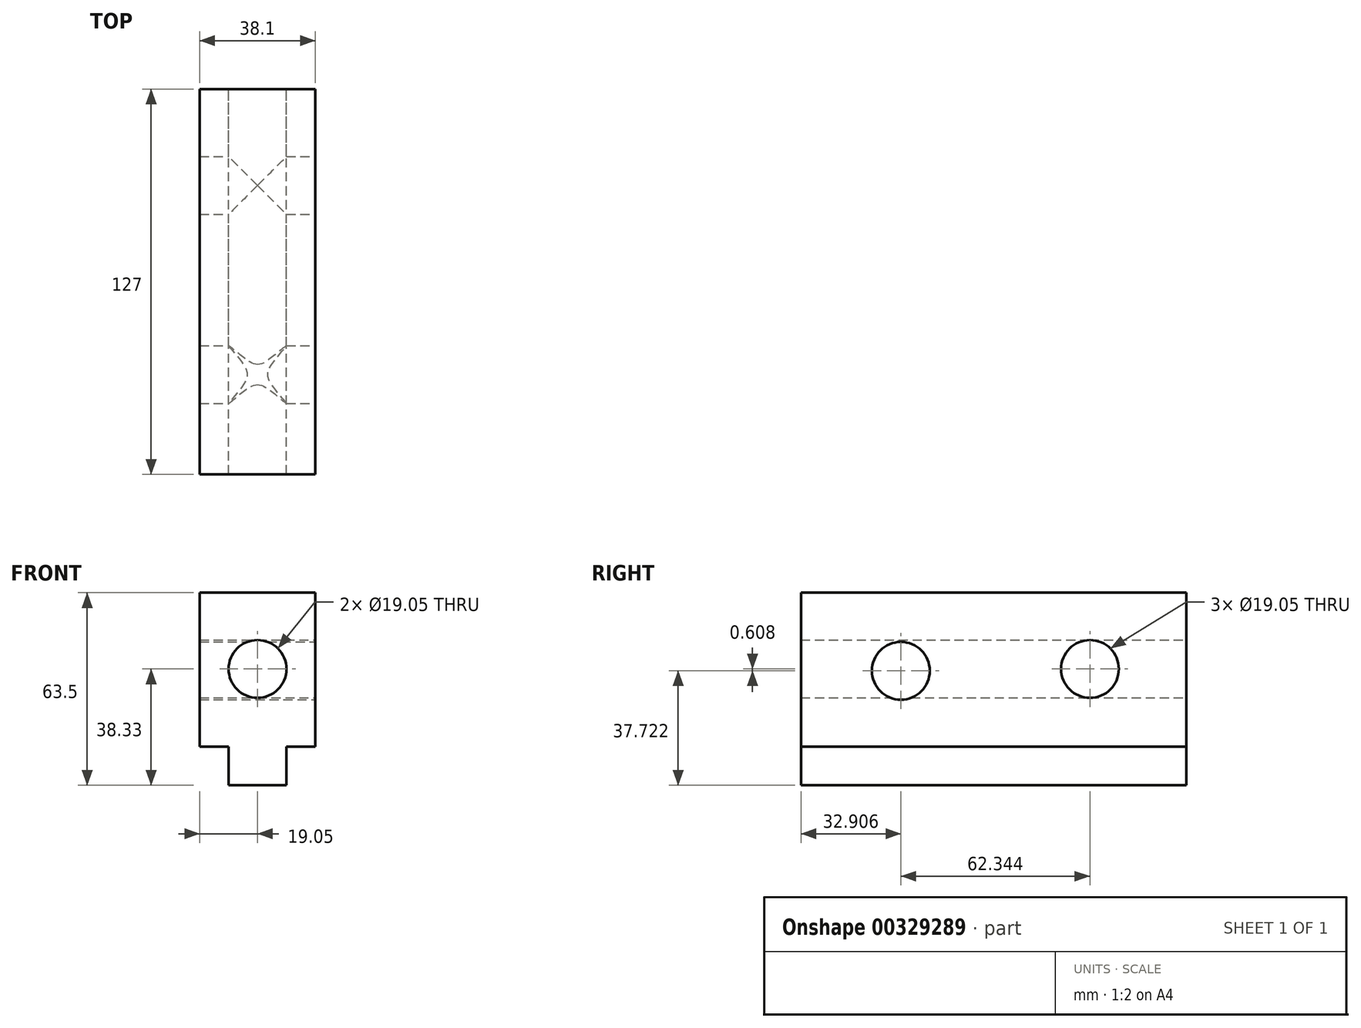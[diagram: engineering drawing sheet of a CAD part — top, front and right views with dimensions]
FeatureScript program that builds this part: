
annotation { "Feature Type Name" : "Feature", "Feature Type Description" : "" }
export const myFeature = defineFeature(function(context is Context, id is Id, definition is map)
    precondition{}
    {
        {
            var Q0;
            Q0=qCreatedBy(makeId("Front.planeOp"),FACE);
            var sketch = newSketch(context, id + "F0", { "sketchPlane" : qUnion([Q0])});
            skLineSegment(sketch, "E0", {"start": v(-28.57, -38.33) * mm, "end": v(-9.53, -38.33) * mm});
            skLineSegment(sketch, "E1", {"start": v(-28.57, -38.33) * mm, "end": v(-28.57, -25.63) * mm});
            skLineSegment(sketch, "E2", {"start": v(-9.53, -38.33) * mm, "end": v(-9.53, -25.63) * mm});
            skLineSegment(sketch, "E3", {"start": v(-9.53, -25.63) * mm, "end": v(0, -25.63) * mm});
            skLineSegment(sketch, "E4", {"start": v(-28.57, -25.63) * mm, "end": v(-38.1, -25.63) * mm});
            skLineSegment(sketch, "E5", {"start": v(-38.1, -25.63) * mm, "end": v(-38.1, 25.17) * mm});
            skLineSegment(sketch, "E6", {"start": v(-38.1, 25.17) * mm, "end": v(0, 25.17) * mm});
            skLineSegment(sketch, "E7", {"start": v(0, -25.63) * mm, "end": v(0, 25.17) * mm});
            skCircle(sketch, "E8", {"center": v(-19.05, 0) * mm, "radius": 9.53 * mm});
            skSolve(sketch);
        }
        {
            var Q0;
            Q0 = qSketchRegion(id + "F0", true);
            extrude(context, id + "F1", {"entities" : qUnion([Q0]), "depth" : 127 * mm});
        }
        {
            var Q0;
            Q0=qCreatedBy(makeId("Right.planeOp"),FACE);
            var sketch = newSketch(context, id + "F2", { "sketchPlane" : qUnion([Q0])});
            skPoint(sketch, "E9", {"position": v(-31.75, 39.15) * mm});
            skPoint(sketch, "E10", {"position": v(0, 39.15) * mm});
            skLineSegment(sketch, "E11", {"start": v(-31.75, 39.15) * mm, "end": v(-31.75, -40.37) * mm});
            skPoint(sketch, "E12", {"position": v(0, 25.4) * mm});
            skPoint(sketch, "E13", {"position": v(0, 0) * mm});
            skCircle(sketch, "E14", {"center": v(-31.75, 0) * mm, "radius": 9.53 * mm});
            skPoint(sketch, "E15", {"position": v(-129.93, 25.5) * mm});
            skPoint(sketch, "E16", {"position": v(-98.18, 25.21) * mm});
            skCircle(sketch, "E17", {"center": v(-94.1, -0.6) * mm, "radius": 9.53 * mm});
            skPoint(sketch, "E17.centerSnap0", {"position": v(-31.75, -0.6) * mm});
            skSolve(sketch);
        }
        {
            var Q0;
            Q0 = qSketchRegion(id + "F2", true);
            extrude(context, id + "F3", {"entities" : qUnion([Q0]), "operationType" : NewBodyOperationType.REMOVE, "oppositeDirection" : true, "depth" : 60.96 * mm});
        }
    });
